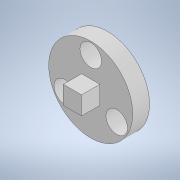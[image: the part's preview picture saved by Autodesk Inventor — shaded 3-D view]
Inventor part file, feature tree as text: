
AUTODESK INVENTOR PART (.ipt)
format: ipt  version: 2022 (Build 260153000, 153)  size: 125,952 bytes
history: native  units: in
note: dims shown in document units (in); Inventor stores cm internally (conversion verified against a paired STEP export)
features: extrude x3, sketch x1
ambient origin geometry x8: Origin, YZ Plane, XZ Plane, XY Plane, X Axis, Y Axis, Z Axis, Center Point
bodies: Solid1 (feature_tree)
feature tree (4):
  extrude  "Extrusion1"  Depth=0.2756in TaperAngle=0.0deg
  extrude  "Extrusion2"  Depth=0.3in
  extrude  "Extrusion4"  Depth=0.3in
  sketch  "Sketch3"  dims[d0=0.9843in d4=0.2756in d5=0.0in d6=0.3543in d7=0.3543in d8=0.3543in d9=0.2756in d10=0.0in d12=0.3543in d14=1.378in d17=0.3in d18=0.3in d19=0.3in d20=0.0in]
